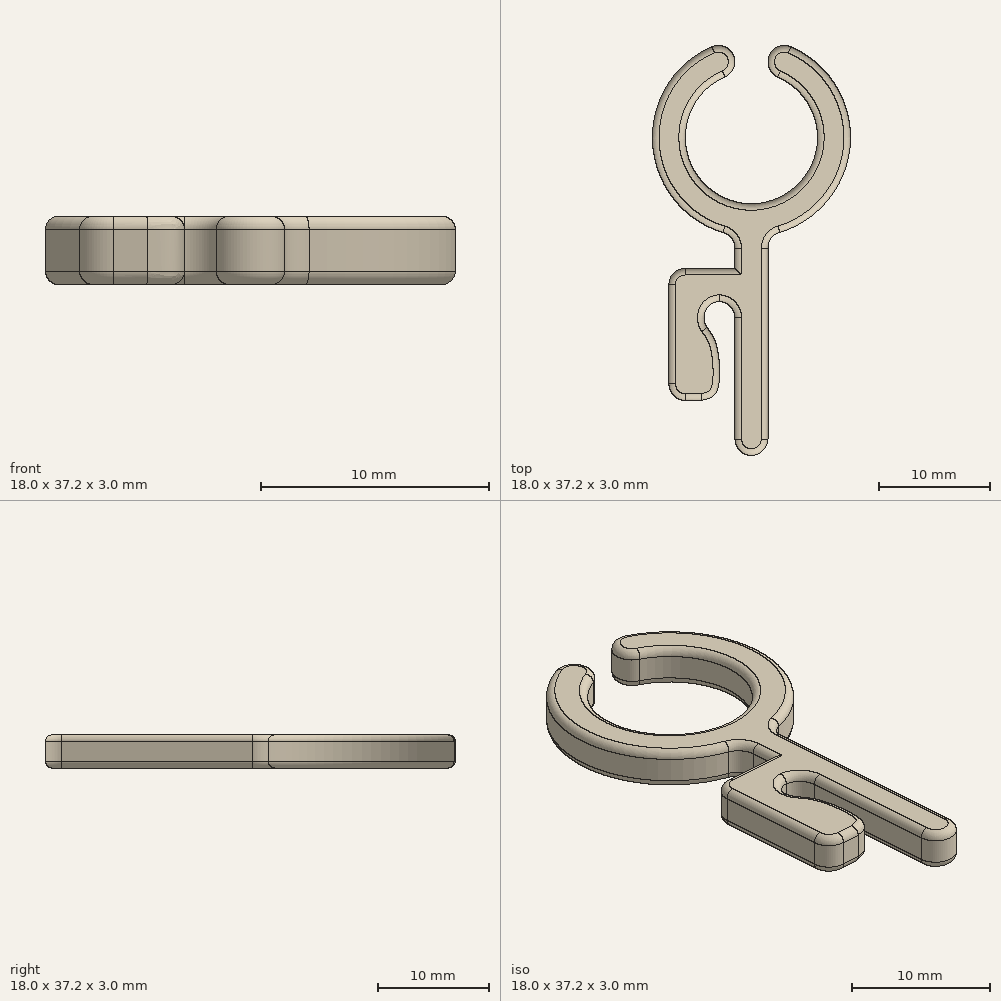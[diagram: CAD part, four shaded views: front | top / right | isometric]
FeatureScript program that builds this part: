
annotation { "Feature Type Name" : "Feature", "Feature Type Description" : "" }
export const myFeature = defineFeature(function(context is Context, id is Id, definition is map)
    precondition{}
    {
        {
            var Q0;
            Q0=qCreatedBy(makeId("Top.planeOp"),FACE);
            var sketch = newSketch(context, id + "F0", { "sketchPlane" : qUnion([Q0])});
            skArc(sketch, "E0", {"start": v(-1.5, 5.8) * mm, "mid": v(0, -6) * mm, "end": v(1.5, 5.8) * mm});
            skArc(sketch, "E1", {"start": v(-1.5, 8.87) * mm, "mid": v(-9, 0) * mm, "end": v(-1.5, -8.87) * mm});
            skLineSegment(sketch, "E2.bottom", {"start": v(1.5, -28.87) * mm, "end": v(-1.5, -28.87) * mm});
            skLineSegment(sketch, "E2.left", {"start": v(1.5, -28.87) * mm, "end": v(1.5, -8.87) * mm});
            skLineSegment(sketch, "E2.right", {"start": v(-1.5, -28.87) * mm, "end": v(-1.5, -8.87) * mm});
            skPoint(sketch, "E3", {"position": v(-1.5, 8.87) * mm});
            skPoint(sketch, "E4", {"position": v(1.5, 8.87) * mm});
            skPoint(sketch, "E5", {"position": v(1.5, 5.8) * mm});
            skPoint(sketch, "E6", {"position": v(-1.5, 5.8) * mm});
            skLineSegment(sketch, "E7.trimOffspring", {"start": v(-1.5, 5.8) * mm, "end": v(-1.5, 8.87) * mm});
            skLineSegment(sketch, "E8.trimOffspring", {"start": v(1.5, 5.8) * mm, "end": v(1.5, 8.87) * mm});
            skArc(sketch, "E9.trimOffspring", {"start": v(1.5, -8.87) * mm, "mid": v(9, 0) * mm, "end": v(1.5, 8.87) * mm});
            skLineSegment(sketch, "E10.bottom", {"start": v(-1.5, -11.87) * mm, "end": v(-7.5, -11.87) * mm});
            skLineSegment(sketch, "E10.top", {"start": v(-1.5, -14.87) * mm, "end": v(-4.5, -14.87) * mm});
            skLineSegment(sketch, "E10.left", {"start": v(-1.5, -11.87) * mm, "end": v(-1.5, -14.87) * mm});
            skLineSegment(sketch, "E11.top", {"start": v(-7.5, -23.87) * mm, "end": v(-4.5, -23.87) * mm});
            skLineSegment(sketch, "E11.left", {"start": v(-7.5, -11.87) * mm, "end": v(-7.5, -23.87) * mm});
            skPoint(sketch, "E12", {"position": v(0, -28.87) * mm});
            skLineSegment(sketch, "E13", {"start": v(-1.5, 5.8) * mm, "end": v(0, 0) * mm, "construction": true});
            skLineSegment(sketch, "E14", {"start": v(1.5, 5.8) * mm, "end": v(0, 0) * mm, "construction": true});
            skLineSegment(sketch, "E15", {"start": v(-1.5, 5.8) * mm, "end": v(1.5, 5.8) * mm, "construction": true});
            skPoint(sketch, "E16", {"position": v(0, 5.8) * mm});
            skFitSpline(sketch, "E17", {"points": [v(-4.5, -23.87) * mm, v(-3.26, -23.28) * mm, v(-2.9, -21) * mm, v(-3.5, -18.06) * mm, v(-4.5, -16.47) * mm, v(-4.5, -14.87) * mm], "startDerivative": vector(10.79, 2.61) * mm, "endDerivative": vector(1.84, 9.76) * mm});
            skSolve(sketch);
        }
        {
            var Q0;
            Q0 = qSketchRegion(id + "F0", true);
            extrude(context, id + "F1", {"entities" : qUnion([Q0]), "depth" : 3 * mm, "offsetDistance" : 25 * mm});
        }
        {
            var Q0;
            Q0=makeQuery(id+"F1.opExtrude","SWEPT_EDGE",EDGE,{"disambiguationData":[OSD([sQuery(id+"F0.wireOp",EDGE,"E2.bottom"),sQuery(id+"F0.wireOp",EDGE,"E2.right")])]});
            var Q1;
            Q1=makeQuery(id+"F1.opExtrude","SWEPT_EDGE",EDGE,{"disambiguationData":[OSD([sQuery(id+"F0.wireOp",EDGE,"E2.bottom"),sQuery(id+"F0.wireOp",EDGE,"E2.left")])]});
            var Q2;
            Q2=makeQuery(id+"F1.opExtrude","SWEPT_EDGE",EDGE,{"disambiguationData":[OSD([sQuery(id+"F0.wireOp",EDGE,"E11.top"),sQuery(id+"F0.wireOp",EDGE,"E11.left")])]});
            var Q3;
            Q3=makeQuery(id+"F1.opExtrude","SWEPT_EDGE",EDGE,{"disambiguationData":[OSD([sQuery(id+"F0.wireOp",EDGE,"E10.top"),sQuery(id+"F0.wireOp",EDGE,"E17")])]});
            var Q4;
            Q4=makeQuery(id+"F1.opExtrude","SWEPT_EDGE",EDGE,{"disambiguationData":[OSD([sQuery(id+"F0.wireOp",EDGE,"E2.left"),sQuery(id+"F0.wireOp",EDGE,"E9.trimOffspring")])]});
            var Q5;
            Q5=makeQuery(id+"F1.opExtrude","SWEPT_EDGE",EDGE,{"disambiguationData":[OSD([sQuery(id+"F0.wireOp",EDGE,"E0"),sQuery(id+"F0.wireOp",EDGE,"E8.trimOffspring")])]});
            var Q6;
            Q6=makeQuery(id+"F1.opExtrude","SWEPT_EDGE",EDGE,{"disambiguationData":[OSD([sQuery(id+"F0.wireOp",EDGE,"E0"),sQuery(id+"F0.wireOp",EDGE,"E7.trimOffspring")])]});
            var Q7;
            Q7=makeQuery(id+"F1.opExtrude","SWEPT_EDGE",EDGE,{"disambiguationData":[OSD([sQuery(id+"F0.wireOp",EDGE,"E1"),sQuery(id+"F0.wireOp",EDGE,"E7.trimOffspring")])]});
            var Q8;
            Q8=makeQuery(id+"F1.opExtrude","SWEPT_EDGE",EDGE,{"disambiguationData":[OSD([sQuery(id+"F0.wireOp",EDGE,"E2.right"),sQuery(id+"F0.wireOp",EDGE,"E10.top"),sQuery(id+"F0.wireOp",EDGE,"E10.left")])]});
            var Q9;
            Q9=makeQuery(id+"F1.opExtrude","SWEPT_EDGE",EDGE,{"disambiguationData":[OSD([sQuery(id+"F0.wireOp",EDGE,"E1"),sQuery(id+"F0.wireOp",EDGE,"E2.right")])]});
            var Q10;
            Q10=makeQuery(id+"F1.opExtrude","SWEPT_EDGE",EDGE,{"disambiguationData":[OSD([sQuery(id+"F0.wireOp",EDGE,"E10.bottom"),sQuery(id+"F0.wireOp",EDGE,"E11.left")])]});
            var Q11;
            Q11=makeQuery(id+"F1.opExtrude","SWEPT_EDGE",EDGE,{"disambiguationData":[OSD([sQuery(id+"F0.wireOp",EDGE,"E8.trimOffspring"),sQuery(id+"F0.wireOp",EDGE,"E9.trimOffspring")])]});
            fillet(context, id + "F2", {"entities" : qUnion([Q0, Q1, Q2, Q3, Q4, Q5, Q6, Q7, Q8, Q9, Q10, Q11]), "radius" : 1.5 * mm, "tangentPropagation" : true, "allowEdgeOverflow" : false});
        }
        {
            var Q0;
            Q0=makeQuery(id+"F1.opExtrude","CAP_FACE",FACE,{"disambiguationData":[OSD([sQuery(id+"F0.wireOp",EDGE,"E0"),sQuery(id+"F0.wireOp",EDGE,"E1"),sQuery(id+"F0.wireOp",EDGE,"E2.bottom"),sQuery(id+"F0.wireOp",EDGE,"E2.left"),sQuery(id+"F0.wireOp",EDGE,"E2.right"),sQuery(id+"F0.wireOp",EDGE,"E7.trimOffspring"),sQuery(id+"F0.wireOp",EDGE,"E8.trimOffspring"),sQuery(id+"F0.wireOp",EDGE,"E9.trimOffspring"),sQuery(id+"F0.wireOp",EDGE,"E10.bottom"),sQuery(id+"F0.wireOp",EDGE,"E10.top"),sQuery(id+"F0.wireOp",EDGE,"E11.top"),sQuery(id+"F0.wireOp",EDGE,"E11.left"),sQuery(id+"F0.wireOp",EDGE,"E17")])],"isStart":false});
            fillet(context, id + "F3", {"entities" : qUnion([Q0]), "radius" : 0.6 * mm, "tangentPropagation" : true, "allowEdgeOverflow" : false});
        }
        {
            var Q0;
            Q0=makeQuery(id+"F1.opExtrude","CAP_FACE",FACE,{"disambiguationData":[OSD([sQuery(id+"F0.wireOp",EDGE,"E0"),sQuery(id+"F0.wireOp",EDGE,"E1"),sQuery(id+"F0.wireOp",EDGE,"E2.bottom"),sQuery(id+"F0.wireOp",EDGE,"E2.left"),sQuery(id+"F0.wireOp",EDGE,"E2.right"),sQuery(id+"F0.wireOp",EDGE,"E7.trimOffspring"),sQuery(id+"F0.wireOp",EDGE,"E8.trimOffspring"),sQuery(id+"F0.wireOp",EDGE,"E9.trimOffspring"),sQuery(id+"F0.wireOp",EDGE,"E10.bottom"),sQuery(id+"F0.wireOp",EDGE,"E10.top"),sQuery(id+"F0.wireOp",EDGE,"E11.top"),sQuery(id+"F0.wireOp",EDGE,"E11.left"),sQuery(id+"F0.wireOp",EDGE,"E17")])],"isStart":true});
            fillet(context, id + "F4", {"entities" : qUnion([Q0]), "radius" : 0.6 * mm, "tangentPropagation" : true, "allowEdgeOverflow" : false});
        }
    });
